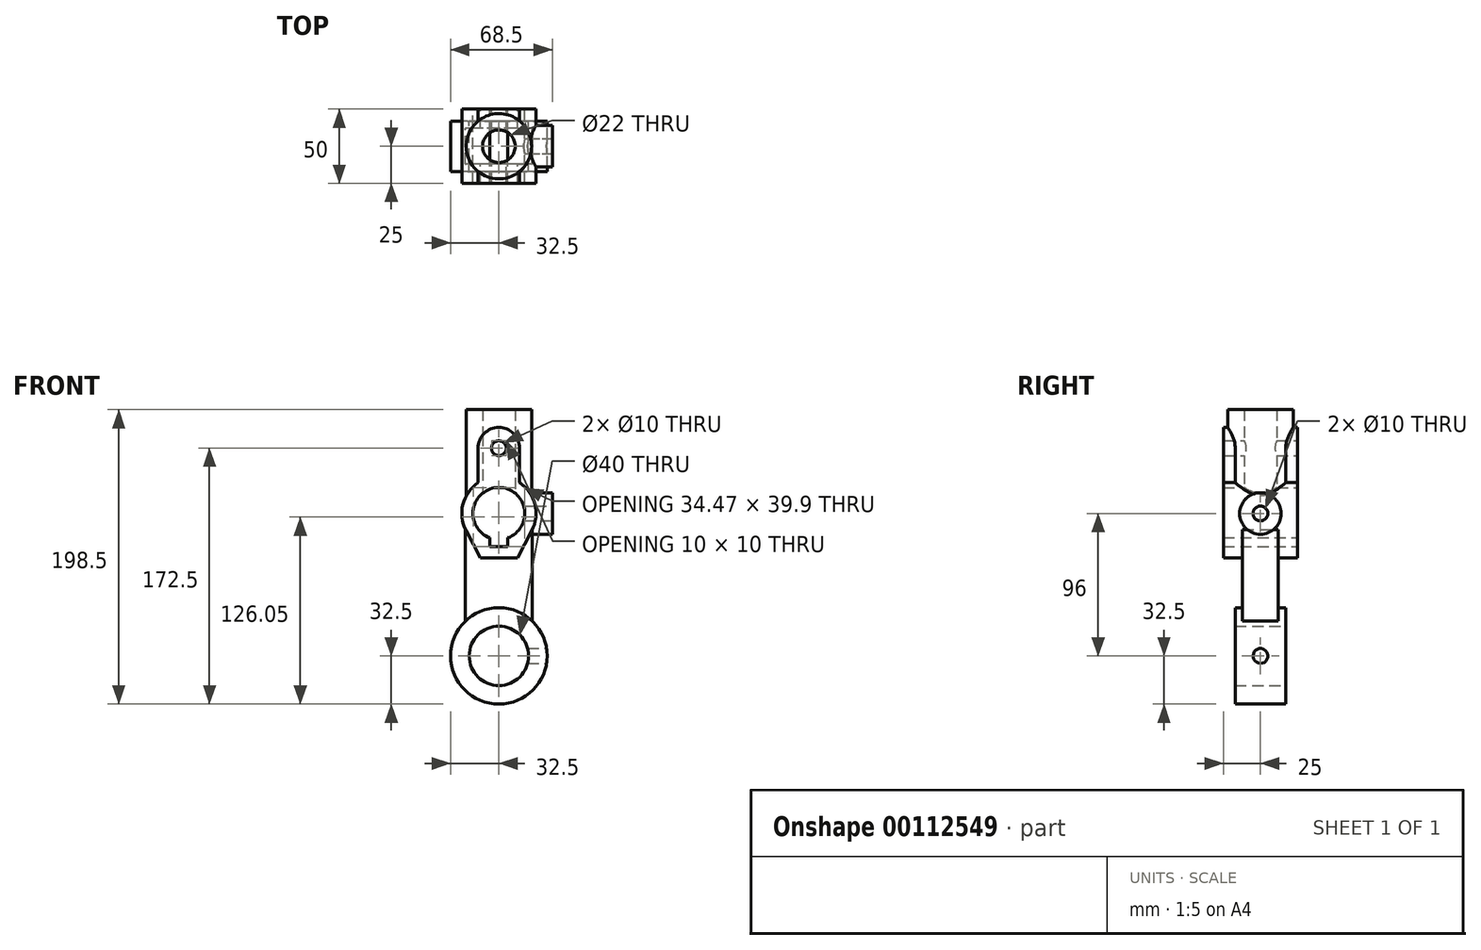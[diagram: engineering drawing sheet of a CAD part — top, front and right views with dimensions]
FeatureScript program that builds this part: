
annotation { "Feature Type Name" : "Feature", "Feature Type Description" : "" }
export const myFeature = defineFeature(function(context is Context, id is Id, definition is map)
    precondition{}
    {
        {
            var Q0;
            Q0=qCreatedBy(makeId("Front.planeOp"),FACE);
            var sketch = newSketch(context, id + "F0", { "sketchPlane" : qUnion([Q0])});
            skArc(sketch, "E0", {"start": v(6, -16.44) * mm, "mid": v(0, 17.5) * mm, "end": v(-6, -16.44) * mm});
            skLineSegment(sketch, "E1", {"start": v(0, -58.53) * mm, "end": v(0, 69.1) * mm, "construction": true});
            skLineSegment(sketch, "E2", {"start": v(-6, -16.44) * mm, "end": v(-6, -22.4) * mm});
            skLineSegment(sketch, "E3", {"start": v(-6, -22.4) * mm, "end": v(0, -22.4) * mm});
            skLineSegment(sketch, "E4.MirrorCS", {"start": v(6, -22.4) * mm, "end": v(0, -22.4) * mm});
            skLineSegment(sketch, "E5.MirrorCS", {"start": v(6, -16.44) * mm, "end": v(6, -22.4) * mm});
            skCircle(sketch, "E6", {"center": v(0, 44) * mm, "radius": 5 * mm});
            skArc(sketch, "E7", {"start": v(14, 44) * mm, "mid": v(0, 58) * mm, "end": v(-14, 44) * mm});
            skArc(sketch, "E8", {"start": v(-14, 20.71) * mm, "mid": v(-24.24, 6.1) * mm, "end": v(-22.14, -11.6) * mm});
            skLineSegment(sketch, "E9", {"start": v(-14, 44) * mm, "end": v(-14, 20.71) * mm});
            skLineSegment(sketch, "E10", {"start": v(14, 44) * mm, "end": v(14, 20.71) * mm});
            skLineSegment(sketch, "E11", {"start": v(0, -30) * mm, "end": v(-12.5, -30) * mm});
            skLineSegment(sketch, "E12", {"start": v(-12.5, -30) * mm, "end": v(-22.14, -11.6) * mm});
            skLineSegment(sketch, "E13.MirrorCS", {"start": v(0, -30) * mm, "end": v(12.5, -30) * mm});
            skLineSegment(sketch, "E14.MirrorCS", {"start": v(12.5, -30) * mm, "end": v(22.14, -11.6) * mm});
            skArc(sketch, "E15.trimOffspring", {"start": v(22.14, -11.6) * mm, "mid": v(24.24, 6.1) * mm, "end": v(14, 20.71) * mm});
            skSolve(sketch);
        }
        {
            var Q0;
            Q0 = qSketchRegion(id + "F0", true);
            extrude(context, id + "F1", {"entities" : qUnion([Q0]), "depth" : 25 * mm, "hasSecondDirection" : true, "secondDirectionOppositeDirection" : true, "secondDirectionDepth" : 25 * mm});
        }
        {
            var Q0;
            Q0=qCreatedBy(makeId("Top.planeOp"),FACE);
            var sketch = newSketch(context, id + "F2", { "sketchPlane" : qUnion([Q0])});
            skLineSegment(sketch, "E16.bottom", {"start": v(-22.5, 12) * mm, "end": v(22.5, 12) * mm});
            skLineSegment(sketch, "E16.top", {"start": v(-22.5, -12) * mm, "end": v(22.5, -12) * mm});
            skLineSegment(sketch, "E16.left", {"start": v(-22.5, 12) * mm, "end": v(-22.5, -12) * mm});
            skLineSegment(sketch, "E16.right", {"start": v(22.5, 12) * mm, "end": v(22.5, -12) * mm});
            skSolve(sketch);
        }
        {
            var Q0;
            Q0 = qSketchRegion(id + "F2", true);
            extrude(context, id + "F3", {"entities" : qUnion([Q0]), "operationType" : NewBodyOperationType.ADD, "oppositeDirection" : true, "depth" : 96 * mm});
        }
        {
            var Q0;
            Q0=qCreatedBy(makeId("Front.planeOp"),FACE);
            var sketch = newSketch(context, id + "F4", { "sketchPlane" : qUnion([Q0])});
            skCircle(sketch, "E17", {"center": v(0, -96) * mm, "radius": 32.5 * mm});
            skCircle(sketch, "E18", {"center": v(0, -96) * mm, "radius": 20 * mm});
            skSolve(sketch);
        }
        {
            var Q0;
            Q0 = qSketchRegion(id + "F4", true);
            extrude(context, id + "F5", {"entities" : qUnion([Q0]), "operationType" : NewBodyOperationType.ADD, "depth" : 17 * mm, "hasSecondDirection" : true, "secondDirectionOppositeDirection" : true, "secondDirectionDepth" : 17 * mm});
        }
        {
            var Q0;
            Q0=qCreatedBy(makeId("Top.planeOp"),FACE);
            var sketch = newSketch(context, id + "F6", { "sketchPlane" : qUnion([Q0])});
            skCircle(sketch, "E19", {"center": v(0, 0) * mm, "radius": 11 * mm});
            skCircle(sketch, "E20", {"center": v(0, 0) * mm, "radius": 22 * mm});
            skSolve(sketch);
        }
        {
            var Q0;
            Q0 = qSketchRegion(id + "F6", true);
            extrude(context, id + "F7", {"entities" : qUnion([Q0]), "operationType" : NewBodyOperationType.ADD, "depth" : 70 * mm});
        }
        {
            var Q0;
            Q0=qCreatedBy(makeId("Right.planeOp"),FACE);
            cPlane(context, id + "F8", {"entities" : qUnion([Q0]), "cplaneType" : CPlaneType.OFFSET, "offset" : 36 * mm, "width" : 150 * mm, "height" : 150 * mm});
        }
        {
            var Q0;
            Q0=qCreatedBy(id+"F8.planeOp",FACE);
            var sketch = newSketch(context, id + "F9", { "sketchPlane" : qUnion([Q0])});
            skCircle(sketch, "E21", {"center": v(0, 0) * mm, "radius": 14 * mm});
            skSolve(sketch);
        }
        {
            var Q0;
            Q0 = qSketchRegion(id + "F9", true);
            extrude(context, id + "F10", {"entities" : qUnion([Q0]), "operationType" : NewBodyOperationType.ADD, "endBound" : BoundingType.UP_TO_NEXT, "oppositeDirection" : true, "depth" : 25 * mm});
        }
        {
            var Q0;
            Q0=makeQuery(id+"F1.opExtrude","CAP_FACE",FACE,{"disambiguationData":[OSD([sQuery(id+"F0.wireOp",EDGE,"E0"),sQuery(id+"F0.wireOp",EDGE,"E2"),sQuery(id+"F0.wireOp",EDGE,"E3"),sQuery(id+"F0.wireOp",EDGE,"E4.MirrorCS"),sQuery(id+"F0.wireOp",EDGE,"E5.MirrorCS"),sQuery(id+"F0.wireOp",EDGE,"E6"),sQuery(id+"F0.wireOp",EDGE,"E7"),sQuery(id+"F0.wireOp",EDGE,"E8"),sQuery(id+"F0.wireOp",EDGE,"E9"),sQuery(id+"F0.wireOp",EDGE,"E10"),sQuery(id+"F0.wireOp",EDGE,"E11"),sQuery(id+"F0.wireOp",EDGE,"E12"),sQuery(id+"F0.wireOp",EDGE,"E13.MirrorCS"),sQuery(id+"F0.wireOp",EDGE,"E14.MirrorCS"),sQuery(id+"F0.wireOp",EDGE,"E15.trimOffspring")])],"isStart":false});
            var sketch = newSketch(context, id + "F11", { "sketchPlane" : qUnion([Q0])});
            skCircle(sketch, "E22.0", {"center": v(0, 44) * mm, "radius": 5 * mm});
            skArc(sketch, "E23.0", {"start": v(6, -16.44) * mm, "mid": v(0, 17.5) * mm, "end": v(-6, -16.44) * mm});
            skLineSegment(sketch, "E23.1", {"start": v(6, -22.4) * mm, "end": v(-6, -22.4) * mm});
            skLineSegment(sketch, "E23.2", {"start": v(6, -16.44) * mm, "end": v(6, -22.4) * mm});
            skLineSegment(sketch, "E23.3", {"start": v(-6, -16.44) * mm, "end": v(-6, -22.4) * mm});
            skCircle(sketch, "E24.0", {"center": v(0, -96) * mm, "radius": 20 * mm});
            skSolve(sketch);
        }
        {
            var Q0;
            Q0 = qSketchRegion(id + "F11", true);
            extrude(context, id + "F12", {"entities" : qUnion([Q0]), "operationType" : NewBodyOperationType.REMOVE, "endBound" : BoundingType.THROUGH_ALL, "oppositeDirection" : true, "depth" : 25 * mm});
        }
        {
            var Q0;
            Q0=makeQuery(id+"F7.opExtrude","CAP_FACE",FACE,{"disambiguationData":[OSD([sQuery(id+"F6.wireOp",EDGE,"E19"),sQuery(id+"F6.wireOp",EDGE,"E20")])],"isStart":false});
            var sketch = newSketch(context, id + "F13", { "sketchPlane" : qUnion([Q0])});
            skCircle(sketch, "E25.0", {"center": v(0, 0) * mm, "radius": 11 * mm});
            skSolve(sketch);
        }
        {
            var Q0;
            Q0 = qSketchRegion(id + "F13", true);
            extrude(context, id + "F14", {"entities" : qUnion([Q0]), "operationType" : NewBodyOperationType.REMOVE, "oppositeDirection" : true, "depth" : 60 * mm});
        }
        {
            var Q0;
            Q0=makeQuery(id+"F10.opExtrude","CAP_FACE",FACE,{"disambiguationData":[OSD([sQuery(id+"F9.wireOp",EDGE,"E21")])],"isStart":true});
            var sketch = newSketch(context, id + "F15", { "sketchPlane" : qUnion([Q0])});
            skCircle(sketch, "E26", {"center": v(0, 0) * mm, "radius": 5 * mm});
            skCircle(sketch, "E27", {"center": v(0, -96) * mm, "radius": 5 * mm});
            skSolve(sketch);
        }
        {
            var Q0;
            Q0 = qSketchRegion(id + "F15", true);
            extrude(context, id + "F16", {"entities" : qUnion([Q0]), "operationType" : NewBodyOperationType.REMOVE, "oppositeDirection" : true, "depth" : 25 * mm});
        }
    });
